# Revit family: Spout-GROHE-Eurosmart-13356_Series
name_source: partatom
category: Plumbing Fixtures
revit_build: Autodesk Revit 2014 (Build: 20130308_1515(x64)
units: mm (PartAtom-declared; Revit-internal decimal feet)

## types (2) — shared parameters
Assembly Code = D2020300
Cold Water Connection Diameter = 1/2"
Cold Water Connection Radius = 1/4"
Default Elevation = 21"
Description = Eurosmart Diverter Tub Spout
Height = 2 7/16"
Hot Water Connection Diameter = 1"
Hot Water Connection Radius = 1/4"
Installation Type = Wall Mounted
Length = 6 3/8"
Manufacturer = Grohe
Price = Prices may vary. Please consult Manufacturer Representative for most up-to-date price list.
Product Page URL = https://www.grohe.us
Shipping Weight = 1.343 lb
Tempered Connection Diameter = 1/2"
Tempered Connection Radius = 1/4"
URL = https://www.grohe.us
Warranty Documentation Link = https://cdn.cloud.grohe.com
Width = 2 7/16"

## per-type parameters (varying)
| type | Finish | Material |
| 13356EN2 | Metal-Grohe-EN2-Brushed Nickel | Metal-Grohe-EN2-Brushed Nickel |
| 13356002 | Metal-Grohe-002-Chrome | Metal-Grohe-002-Chrome |

note: column(s) folded — value = type name in every type: Model

## geometry (parser evidence)
native form markers: Sweep x3
no freeform markers — native parametric forms only
